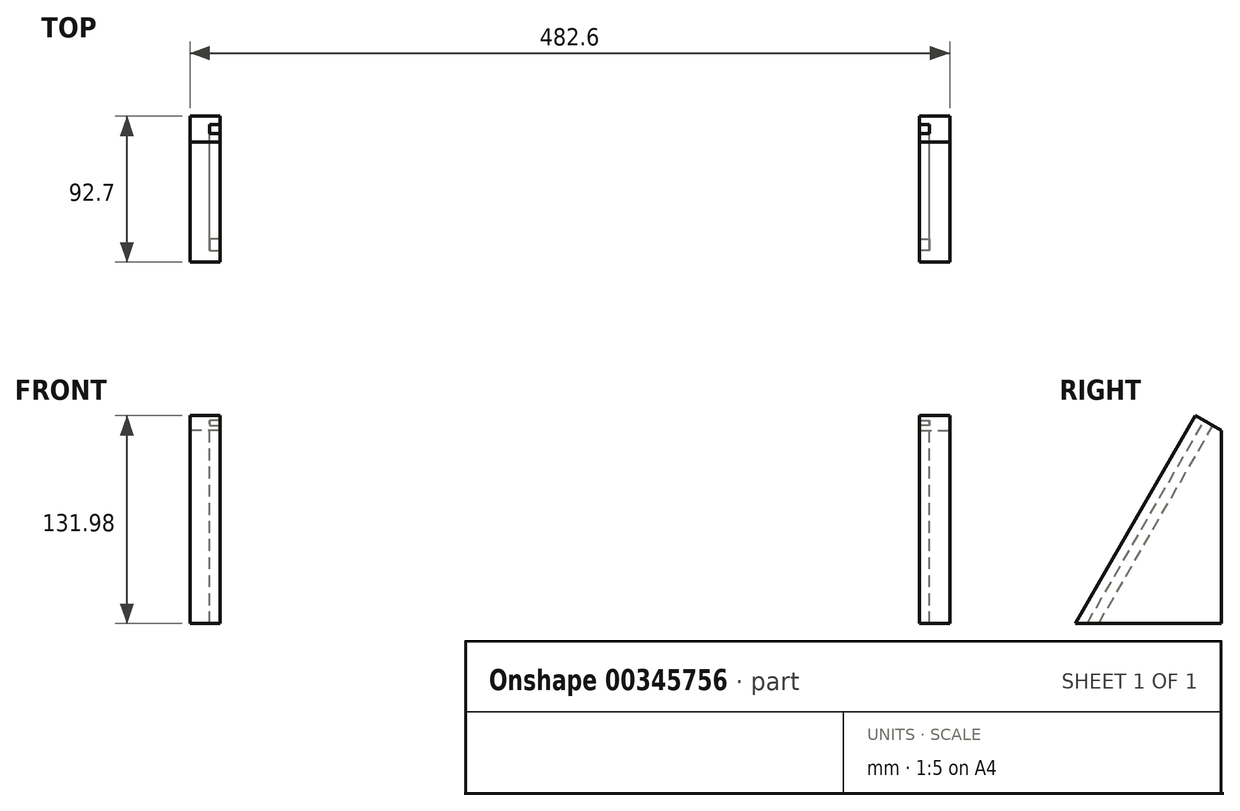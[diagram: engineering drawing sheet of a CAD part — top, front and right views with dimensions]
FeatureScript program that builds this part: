
annotation { "Feature Type Name" : "Feature", "Feature Type Description" : "" }
export const myFeature = defineFeature(function(context is Context, id is Id, definition is map)
    precondition{}
    {
        {
            var Q0;
            Q0=qCreatedBy(makeId("Right.planeOp"),FACE);
            var sketch = newSketch(context, id + "F0", { "sketchPlane" : qUnion([Q0])});
            skLineSegment(sketch, "E0", {"start": v(0, 0) * mm, "end": v(-92.7, 0) * mm});
            skLineSegment(sketch, "E1", {"start": v(-92.7, 0) * mm, "end": v(-16.5, 131.98) * mm});
            skLineSegment(sketch, "E2", {"start": v(-16.5, 131.98) * mm, "end": v(0, 122.46) * mm});
            skLineSegment(sketch, "E3", {"start": v(0, 122.46) * mm, "end": v(0, 0) * mm});
            skSolve(sketch);
        }
        {
            var Q0;
            Q0 = qSketchRegion(id + "F0", true);
            extrude(context, id + "F1", {"entities" : qUnion([Q0]), "depth" : 19.05 * mm});
        }
        {
            var Q0;
            Q0=makeQuery(id+"F1.opExtrude","SWEPT_FACE",FACE,{"disambiguationData":[OSD([sQuery(id+"F0.wireOp",EDGE,"E2")])]});
            cPlane(context, id + "F2", {"entities" : qUnion([Q0]), "cplaneType" : CPlaneType.OFFSET, "offset" : 0 * mm, "width" : 152.4 * mm, "height" : 152.4 * mm});
        }
        {
            var Q0;
            Q0=makeQuery(id+"F1.opExtrude","SWEPT_FACE",FACE,{"disambiguationData":[OSD([sQuery(id+"F0.wireOp",EDGE,"E1")])]});
            cPlane(context, id + "F3", {"entities" : qUnion([Q0]), "cplaneType" : CPlaneType.OFFSET, "offset" : 0 * mm, "width" : 152.4 * mm, "height" : 152.4 * mm});
        }
        {
            var Q0;
            Q0=makeQuery(id+"F1.opExtrude","CAP_FACE",FACE,{"disambiguationData":[OSD([sQuery(id+"F0.wireOp",EDGE,"E0"),sQuery(id+"F0.wireOp",EDGE,"E1"),sQuery(id+"F0.wireOp",EDGE,"E2"),sQuery(id+"F0.wireOp",EDGE,"E3")])],"isStart":false});
            cPlane(context, id + "F4", {"entities" : qUnion([Q0]), "cplaneType" : CPlaneType.OFFSET, "offset" : 0 * mm, "width" : 152.4 * mm, "height" : 152.4 * mm});
        }
        {
            var Q0;
            Q0=qCreatedBy(id+"F2.planeOp",FACE);
            var sketch = newSketch(context, id + "F5", { "sketchPlane" : qUnion([Q0])});
            skLineSegment(sketch, "E4", {"start": v(19.05, -73.93) * mm, "end": v(12.7, -73.93) * mm});
            skLineSegment(sketch, "E5", {"start": v(12.7, -73.93) * mm, "end": v(12.7, -67.58) * mm});
            skLineSegment(sketch, "E6", {"start": v(12.7, -67.58) * mm, "end": v(19.05, -67.58) * mm});
            skLineSegment(sketch, "E7", {"start": v(19.05, -67.58) * mm, "end": v(19.05, -73.93) * mm});
            skLineSegment(sketch, "E8", {"start": v(19.05, -73.93) * mm, "end": v(19.05, -80.28) * mm, "construction": true});
            skSolve(sketch);
        }
        {
            var Q0;
            Q0 = qSketchRegion(id + "F5", true);
            extrude(context, id + "F6", {"entities" : qUnion([Q0]), "operationType" : NewBodyOperationType.REMOVE, "oppositeDirection" : true, "depth" : 152.4 * mm});
        }
        {
            var Q0;
            Q0=qCreatedBy(makeId("Right.planeOp"),FACE);
            cPlane(context, id + "F7", {"entities" : qUnion([Q0]), "cplaneType" : CPlaneType.OFFSET, "offset" : 241.3 * mm, "width" : 152.4 * mm, "height" : 152.4 * mm});
        }
        {
            var Q0;
            Q0=makeQuery(id+"F1.opExtrude","SWEPT_BODY",BODY,{"disambiguationData":[OSD([sQuery(id+"F0.wireOp",EDGE,"E0"),sQuery(id+"F0.wireOp",EDGE,"E1"),sQuery(id+"F0.wireOp",EDGE,"E2"),sQuery(id+"F0.wireOp",EDGE,"E3")])]});
            var Q1;
            Q1=qCreatedBy(id+"F7.planeOp",FACE);
            mirror(context, id + "F8", {"entities" : qUnion([Q0]), "mirrorPlane" : qUnion([Q1])});
        }
    });
